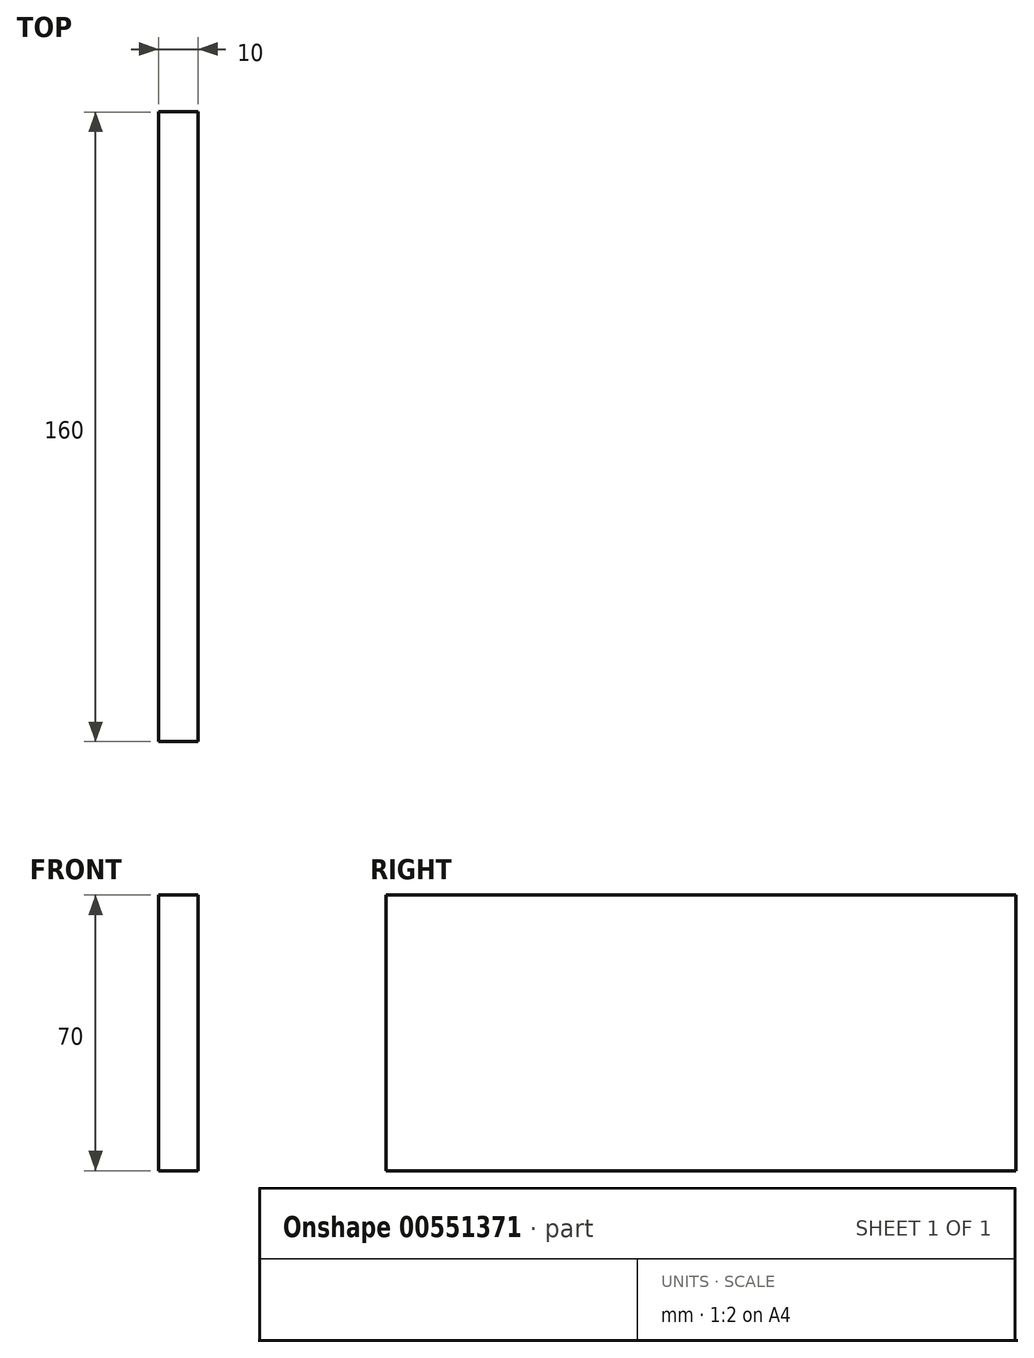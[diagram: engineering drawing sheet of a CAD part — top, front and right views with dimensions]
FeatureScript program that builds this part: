
annotation { "Feature Type Name" : "Feature", "Feature Type Description" : "" }
export const myFeature = defineFeature(function(context is Context, id is Id, definition is map)
    precondition{}
    {
        {
            var Q0;
            Q0=qCreatedBy(makeId("Right.planeOp"),FACE);
            var sketch = newSketch(context, id + "F0", { "sketchPlane" : qUnion([Q0])});
            skLineSegment(sketch, "E0.bottom", {"start": v(-84, 38.9) * mm, "end": v(76, 38.9) * mm});
            skLineSegment(sketch, "E0.top", {"start": v(-84, -31.1) * mm, "end": v(76, -31.1) * mm});
            skLineSegment(sketch, "E0.left", {"start": v(-84, 38.9) * mm, "end": v(-84, -31.1) * mm});
            skLineSegment(sketch, "E0.right", {"start": v(76, 38.9) * mm, "end": v(76, -31.1) * mm});
            skSolve(sketch);
        }
        {
            var Q0;
            Q0 = qSketchRegion(id + "F0", true);
            extrude(context, id + "F1", {"entities" : qUnion([Q0]), "depth" : 10 * mm, "offsetDistance" : 25 * mm});
        }
    });
